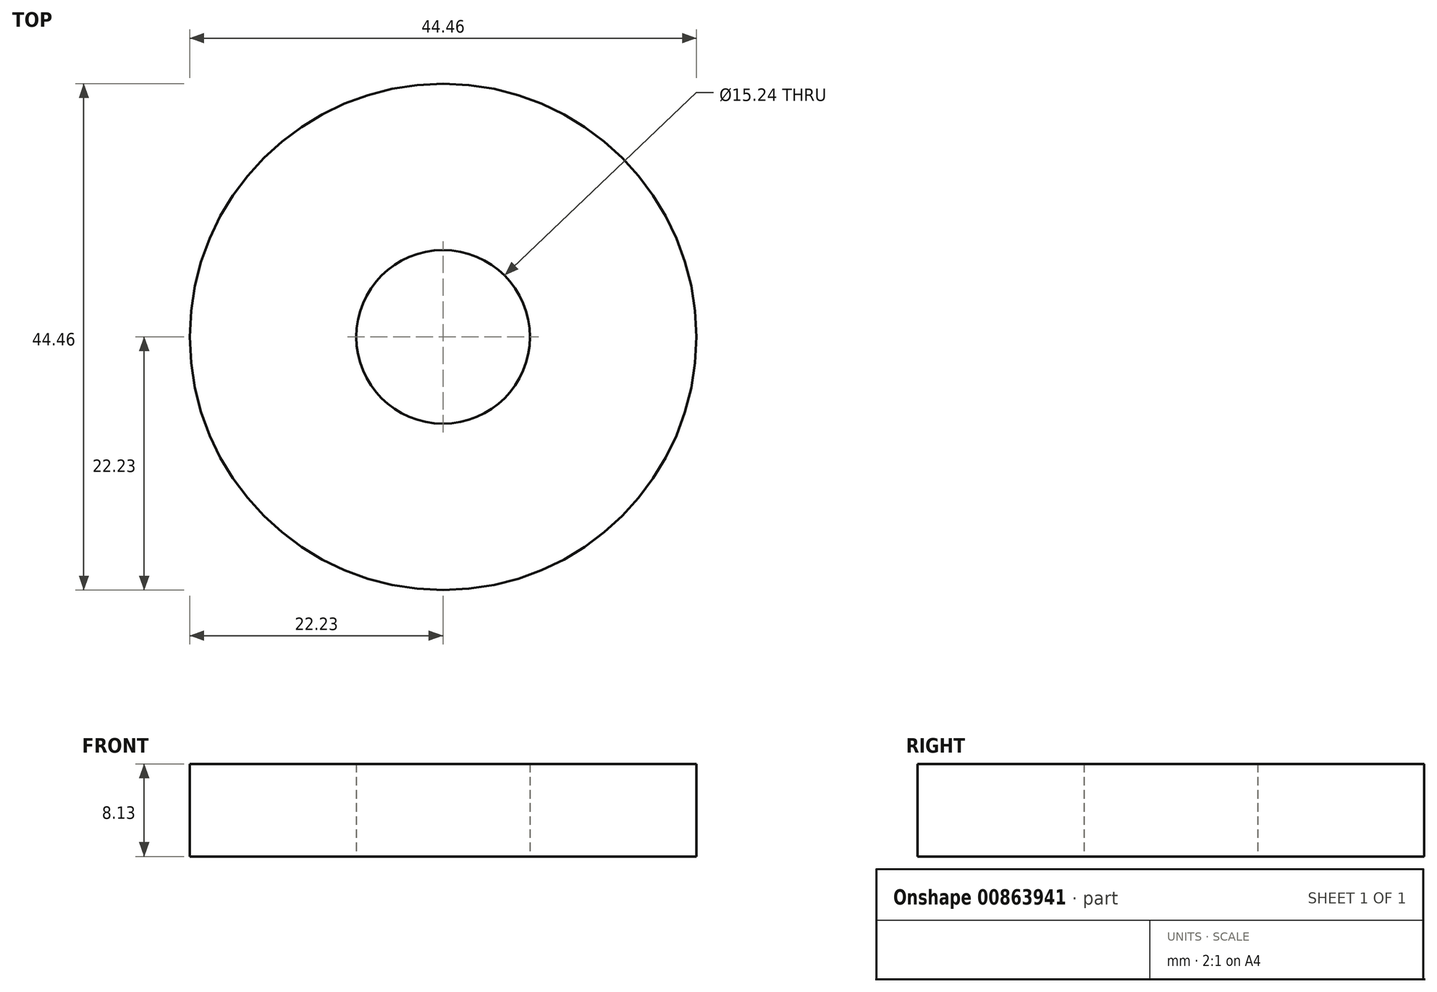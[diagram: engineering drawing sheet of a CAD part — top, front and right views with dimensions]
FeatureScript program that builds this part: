
annotation { "Feature Type Name" : "Feature", "Feature Type Description" : "" }
export const myFeature = defineFeature(function(context is Context, id is Id, definition is map)
    precondition{}
    {
        {
            var Q0;
            Q0=qCreatedBy(makeId("Top.planeOp"),FACE);
            var sketch = newSketch(context, id + "F0", { "sketchPlane" : qUnion([Q0])});
            skCircle(sketch, "E0", {"center": v(0, 0) * mm, "radius": 7.62 * mm});
            skCircle(sketch, "E1", {"center": v(0, 0) * mm, "radius": 22.23 * mm});
            skSolve(sketch);
        }
        {
            var Q0;
            Q0 = qSketchRegion(id + "F0", true);
            extrude(context, id + "F1", {"entities" : qUnion([Q0]), "depth" : 8.13 * mm, "offsetDistance" : 25.4 * mm});
        }
    });
